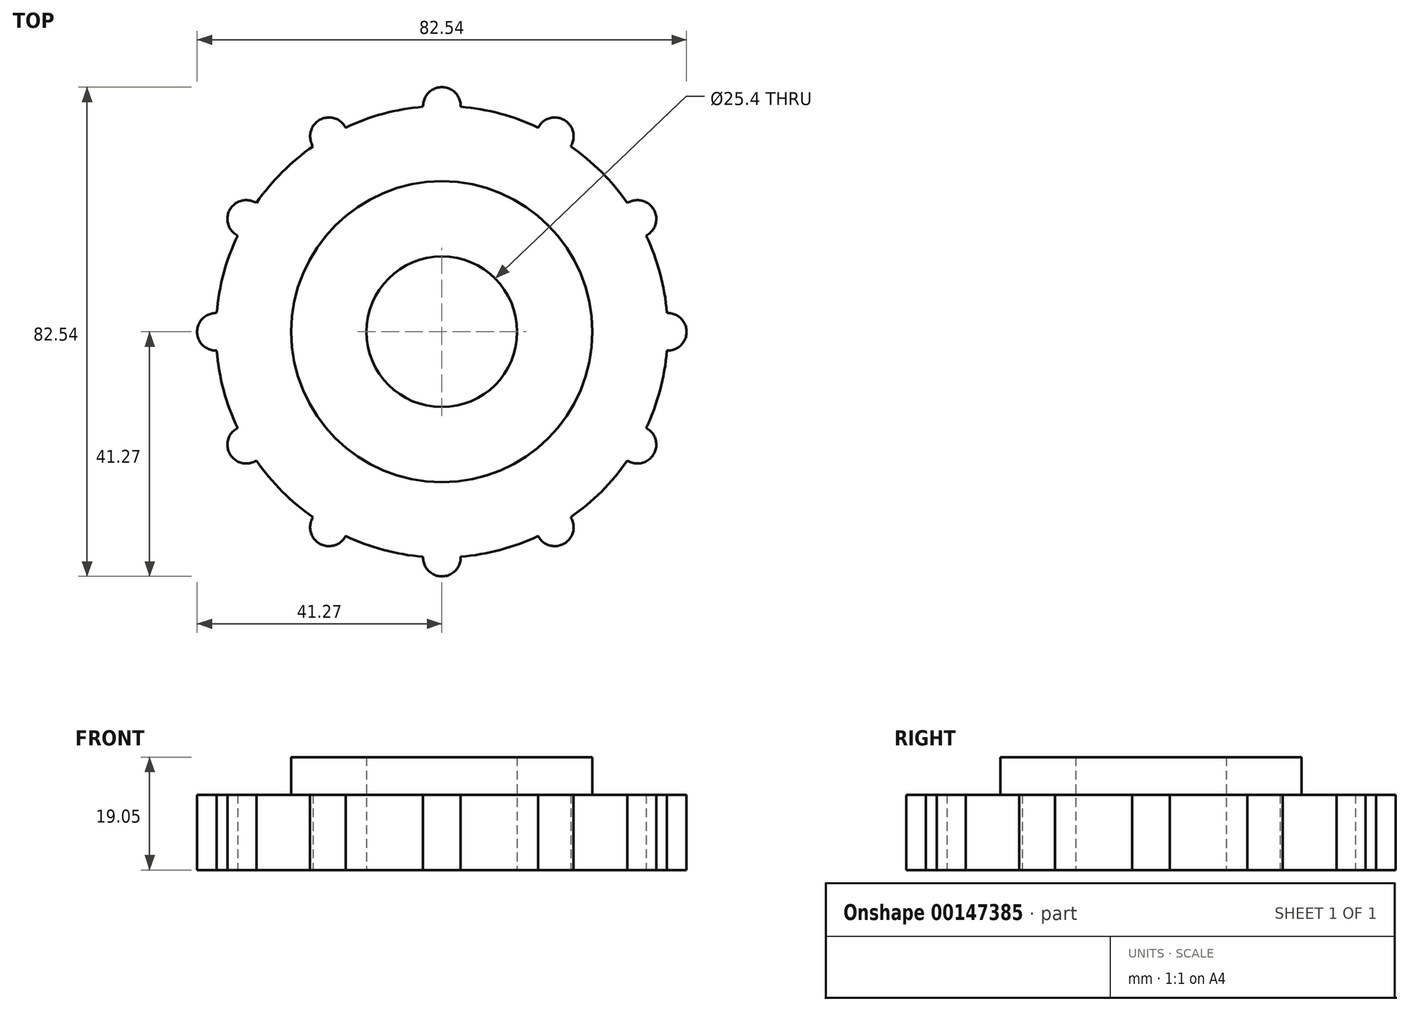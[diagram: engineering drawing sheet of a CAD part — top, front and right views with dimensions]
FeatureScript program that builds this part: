
annotation { "Feature Type Name" : "Feature", "Feature Type Description" : "" }
export const myFeature = defineFeature(function(context is Context, id is Id, definition is map)
    precondition{}
    {
        {
            var Q0;
            Q0=qCreatedBy(makeId("Top.planeOp"),FACE);
            var sketch = newSketch(context, id + "F0", { "sketchPlane" : qUnion([Q0])});
            skCircle(sketch, "E0", {"center": v(0, 0) * mm, "radius": 38.1 * mm});
            skCircle(sketch, "E1", {"center": v(0, 0) * mm, "radius": 25.4 * mm});
            skCircle(sketch, "E2", {"center": v(0, 0) * mm, "radius": 12.7 * mm});
            skCircle(sketch, "E3", {"center": v(0, 38.1) * mm, "radius": 3.18 * mm});
            skCircle(sketch, "E4.1.0", {"center": v(-19.05, 33) * mm, "radius": 3.18 * mm});
            skCircle(sketch, "E4.2.0", {"center": v(-33, 19.05) * mm, "radius": 3.18 * mm});
            skCircle(sketch, "E4.3.0", {"center": v(-38.1, 0) * mm, "radius": 3.18 * mm});
            skCircle(sketch, "E4.4.0", {"center": v(-33, -19.05) * mm, "radius": 3.18 * mm});
            skCircle(sketch, "E4.5.0", {"center": v(-19.05, -33) * mm, "radius": 3.18 * mm});
            skCircle(sketch, "E4.6.0", {"center": v(0, -38.1) * mm, "radius": 3.18 * mm});
            skCircle(sketch, "E4.7.0", {"center": v(19.05, -33) * mm, "radius": 3.18 * mm});
            skCircle(sketch, "E4.8.0", {"center": v(33, -19.05) * mm, "radius": 3.18 * mm});
            skCircle(sketch, "E4.9.0", {"center": v(38.1, 0) * mm, "radius": 3.18 * mm});
            skCircle(sketch, "E4.10.0", {"center": v(33, 19.05) * mm, "radius": 3.18 * mm});
            skCircle(sketch, "E4.11.0", {"center": v(19.05, 33) * mm, "radius": 3.18 * mm});
            skSolve(sketch);
        }
        {
            var Q0;
            Q0 = qSketchRegion(id + "F0", true);
            extrude(context, id + "F1", {"entities" : qUnion([Q0]), "depth" : 12.7 * mm});
        }
        {
            var Q0;
            Q0=makeQuery(id+"F0.imprint","IMPRINT",FACE,{"disambiguationData":[TD([[makeQuery(id+"F0.imprint","IMPRINT",EDGE,{"derivedFrom":sQuery(id+"F0.wireOp",EDGE,"E1")}),1.0]])]});
            extrude(context, id + "F2", {"entities" : qUnion([Q0]), "operationType" : NewBodyOperationType.ADD, "depth" : 19.05 * mm});
        }
    });
